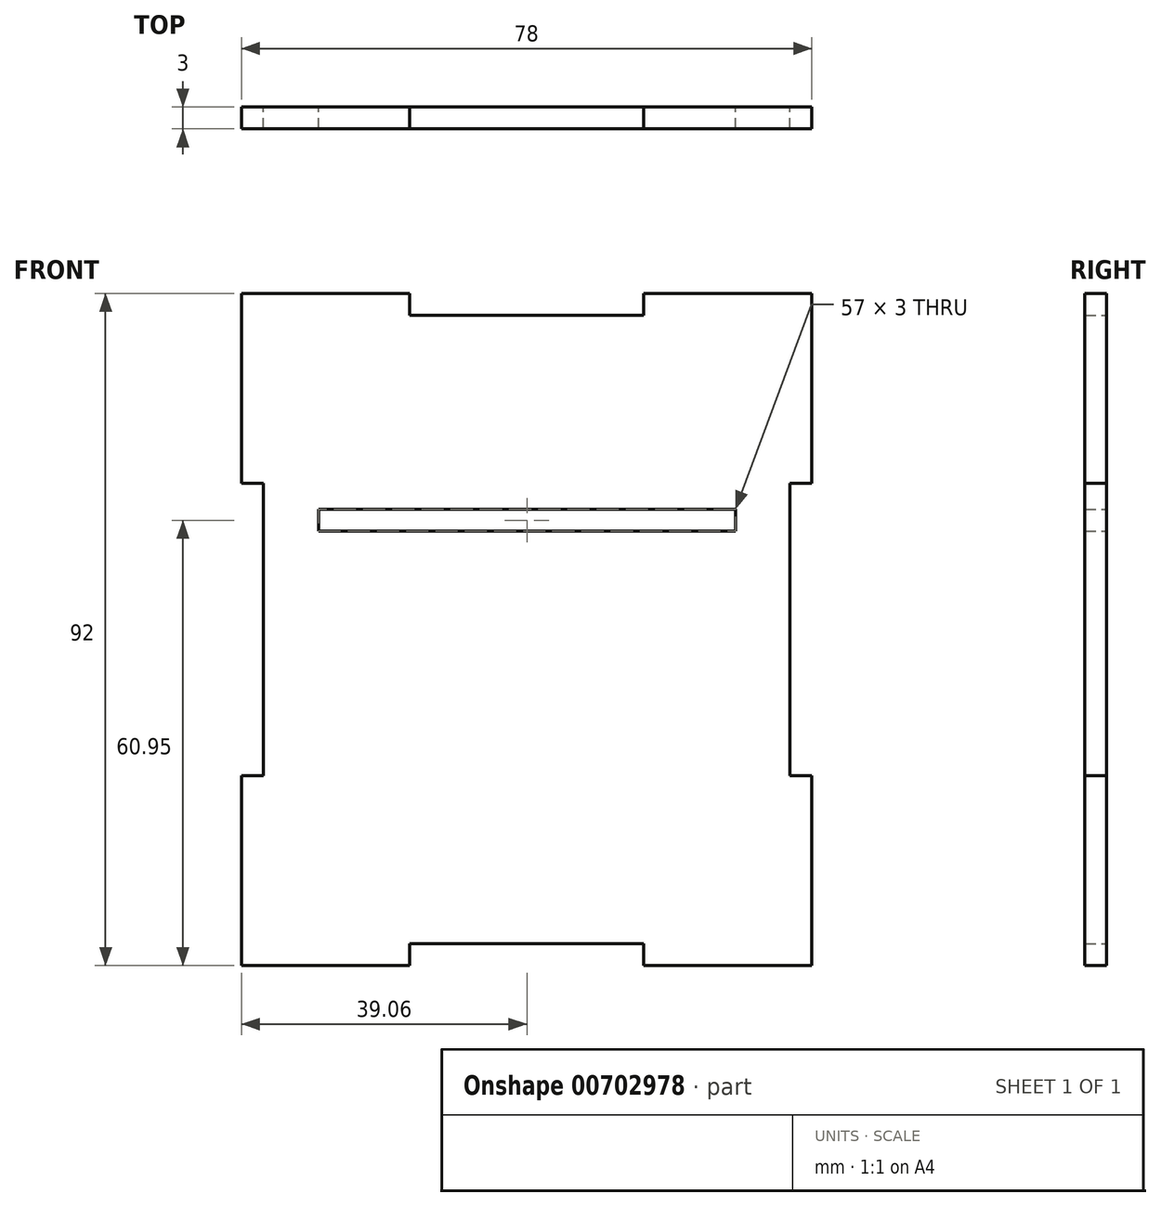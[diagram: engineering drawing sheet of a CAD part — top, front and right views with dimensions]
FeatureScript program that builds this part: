
annotation { "Feature Type Name" : "Feature", "Feature Type Description" : "" }
export const myFeature = defineFeature(function(context is Context, id is Id, definition is map)
    precondition{}
    {
        {
            var Q0;
            Q0=qCreatedBy(makeId("Front.planeOp"),FACE);
            var sketch = newSketch(context, id + "F0", { "sketchPlane" : qUnion([Q0])});
            skLineSegment(sketch, "E0.bottom", {"start": v(35.94, -39.95) * mm, "end": v(-36.06, -39.95) * mm});
            skLineSegment(sketch, "E0.top", {"start": v(35.94, 40.05) * mm, "end": v(-36.06, 40.05) * mm});
            skLineSegment(sketch, "E0.left", {"start": v(35.94, -39.95) * mm, "end": v(35.94, 40.05) * mm});
            skLineSegment(sketch, "E0.right", {"start": v(-36.06, -39.95) * mm, "end": v(-36.06, 40.05) * mm});
            skPoint(sketch, "E0.middle", {"position": v(-0.06, 0.05) * mm});
            skLineSegment(sketch, "E1.bottom", {"start": v(-36.06, 40.05) * mm, "end": v(-16.06, 40.05) * mm, "construction": true});
            skLineSegment(sketch, "E1.top", {"start": v(-36.06, 20.05) * mm, "end": v(-16.06, 20.05) * mm, "construction": true});
            skLineSegment(sketch, "E1.left", {"start": v(-36.06, 40.05) * mm, "end": v(-36.06, 20.05) * mm, "construction": true});
            skLineSegment(sketch, "E1.right", {"start": v(-16.06, 40.05) * mm, "end": v(-16.06, 20.05) * mm, "construction": true});
            skLineSegment(sketch, "E2.bottom", {"start": v(35.94, -39.95) * mm, "end": v(15.94, -39.95) * mm, "construction": true});
            skLineSegment(sketch, "E2.top", {"start": v(35.94, -19.95) * mm, "end": v(15.94, -19.95) * mm, "construction": true});
            skLineSegment(sketch, "E2.left", {"start": v(35.94, -39.95) * mm, "end": v(35.94, -19.95) * mm, "construction": true});
            skLineSegment(sketch, "E2.right", {"start": v(15.94, -39.95) * mm, "end": v(15.94, -19.95) * mm, "construction": true});
            skLineSegment(sketch, "E3.bottom", {"start": v(35.94, 40.05) * mm, "end": v(15.94, 40.05) * mm, "construction": true});
            skLineSegment(sketch, "E3.top", {"start": v(35.94, 20.05) * mm, "end": v(15.94, 20.05) * mm, "construction": true});
            skLineSegment(sketch, "E3.left", {"start": v(35.94, 40.05) * mm, "end": v(35.94, 20.05) * mm, "construction": true});
            skLineSegment(sketch, "E3.right", {"start": v(15.94, 40.05) * mm, "end": v(15.94, 20.05) * mm, "construction": true});
            skLineSegment(sketch, "E4.bottom", {"start": v(-36.06, -39.95) * mm, "end": v(-16.06, -39.95) * mm, "construction": true});
            skLineSegment(sketch, "E4.top", {"start": v(-36.06, -19.95) * mm, "end": v(-16.06, -19.95) * mm, "construction": true});
            skLineSegment(sketch, "E4.left", {"start": v(-36.06, -39.95) * mm, "end": v(-36.06, -19.95) * mm, "construction": true});
            skLineSegment(sketch, "E4.right", {"start": v(-16.06, -39.95) * mm, "end": v(-16.06, -19.95) * mm, "construction": true});
            skLineSegment(sketch, "E5.bottom", {"start": v(-16.06, 40.05) * mm, "end": v(-36.06, 40.05) * mm});
            skLineSegment(sketch, "E5.top", {"start": v(-16.06, 43.05) * mm, "end": v(-36.06, 43.05) * mm});
            skLineSegment(sketch, "E5.left", {"start": v(-16.06, 40.05) * mm, "end": v(-16.06, 43.05) * mm});
            skLineSegment(sketch, "E5.right", {"start": v(-36.06, 40.05) * mm, "end": v(-36.06, 43.05) * mm});
            skLineSegment(sketch, "E6.bottom", {"start": v(35.94, 40.05) * mm, "end": v(15.94, 40.05) * mm});
            skLineSegment(sketch, "E6.top", {"start": v(35.94, 43.05) * mm, "end": v(15.94, 43.05) * mm});
            skLineSegment(sketch, "E6.left", {"start": v(35.94, 40.05) * mm, "end": v(35.94, 43.05) * mm});
            skLineSegment(sketch, "E6.right", {"start": v(15.94, 40.05) * mm, "end": v(15.94, 43.05) * mm});
            skLineSegment(sketch, "E7.bottom", {"start": v(35.94, 40.05) * mm, "end": v(38.94, 40.05) * mm});
            skLineSegment(sketch, "E7.top", {"start": v(35.94, 20.05) * mm, "end": v(38.94, 20.05) * mm});
            skLineSegment(sketch, "E7.left", {"start": v(35.94, 40.05) * mm, "end": v(35.94, 20.05) * mm});
            skLineSegment(sketch, "E7.right", {"start": v(38.94, 40.05) * mm, "end": v(38.94, 20.05) * mm});
            skLineSegment(sketch, "E8.bottom", {"start": v(35.94, -19.95) * mm, "end": v(38.94, -19.95) * mm});
            skLineSegment(sketch, "E8.top", {"start": v(35.94, -39.95) * mm, "end": v(38.94, -39.95) * mm});
            skLineSegment(sketch, "E8.left", {"start": v(35.94, -19.95) * mm, "end": v(35.94, -39.95) * mm});
            skLineSegment(sketch, "E8.right", {"start": v(38.94, -19.95) * mm, "end": v(38.94, -39.95) * mm});
            skLineSegment(sketch, "E9.bottom", {"start": v(-36.06, 40.05) * mm, "end": v(-39.06, 40.05) * mm});
            skLineSegment(sketch, "E9.top", {"start": v(-36.06, 20.05) * mm, "end": v(-39.06, 20.05) * mm});
            skLineSegment(sketch, "E9.left", {"start": v(-36.06, 40.05) * mm, "end": v(-36.06, 20.05) * mm});
            skLineSegment(sketch, "E9.right", {"start": v(-39.06, 40.05) * mm, "end": v(-39.06, 20.05) * mm});
            skLineSegment(sketch, "E10.bottom", {"start": v(-36.06, -19.95) * mm, "end": v(-39.06, -19.95) * mm});
            skLineSegment(sketch, "E10.top", {"start": v(-36.06, -39.95) * mm, "end": v(-39.06, -39.95) * mm});
            skLineSegment(sketch, "E10.left", {"start": v(-36.06, -19.95) * mm, "end": v(-36.06, -39.95) * mm});
            skLineSegment(sketch, "E10.right", {"start": v(-39.06, -19.95) * mm, "end": v(-39.06, -39.95) * mm});
            skLineSegment(sketch, "E11.bottom", {"start": v(-36.06, -39.95) * mm, "end": v(-16.06, -39.95) * mm});
            skLineSegment(sketch, "E11.top", {"start": v(-36.06, -42.95) * mm, "end": v(-16.06, -42.95) * mm});
            skLineSegment(sketch, "E11.left", {"start": v(-36.06, -39.95) * mm, "end": v(-36.06, -42.95) * mm});
            skLineSegment(sketch, "E11.right", {"start": v(-16.06, -39.95) * mm, "end": v(-16.06, -42.95) * mm});
            skLineSegment(sketch, "E12.bottom", {"start": v(15.94, -39.95) * mm, "end": v(35.94, -39.95) * mm});
            skLineSegment(sketch, "E12.top", {"start": v(15.94, -42.95) * mm, "end": v(35.94, -42.95) * mm});
            skLineSegment(sketch, "E12.left", {"start": v(15.94, -39.95) * mm, "end": v(15.94, -42.95) * mm});
            skLineSegment(sketch, "E12.right", {"start": v(35.94, -39.95) * mm, "end": v(35.94, -42.95) * mm});
            skLineSegment(sketch, "E13.top", {"start": v(-36.06, 43.05) * mm, "end": v(-39.06, 43.05) * mm});
            skLineSegment(sketch, "E13.right", {"start": v(-39.06, 40.05) * mm, "end": v(-39.06, 43.05) * mm});
            skLineSegment(sketch, "E14.top", {"start": v(35.94, 43.05) * mm, "end": v(38.94, 43.05) * mm});
            skLineSegment(sketch, "E14.right", {"start": v(38.94, 40.05) * mm, "end": v(38.94, 43.05) * mm});
            skLineSegment(sketch, "E15.top", {"start": v(35.94, -42.95) * mm, "end": v(38.94, -42.95) * mm});
            skLineSegment(sketch, "E15.right", {"start": v(38.94, -39.95) * mm, "end": v(38.94, -42.95) * mm});
            skLineSegment(sketch, "E16.top", {"start": v(-36.06, -42.95) * mm, "end": v(-39.06, -42.95) * mm});
            skLineSegment(sketch, "E16.right", {"start": v(-39.06, -39.95) * mm, "end": v(-39.06, -42.95) * mm});
            skLineSegment(sketch, "E17", {"start": v(35.94, 43.05) * mm, "end": v(35.94, 46.05) * mm});
            skLineSegment(sketch, "E18", {"start": v(35.94, 46.05) * mm, "end": v(15.94, 46.05) * mm});
            skLineSegment(sketch, "E19", {"start": v(15.94, 46.05) * mm, "end": v(15.94, 43.05) * mm});
            skLineSegment(sketch, "E20", {"start": v(-39.06, 43.05) * mm, "end": v(-39.06, 46.05) * mm});
            skLineSegment(sketch, "E21", {"start": v(-39.06, 46.05) * mm, "end": v(-16.06, 46.05) * mm});
            skLineSegment(sketch, "E22", {"start": v(-16.06, 46.05) * mm, "end": v(-16.06, 43.05) * mm});
            skLineSegment(sketch, "E23", {"start": v(-16.06, 43.05) * mm, "end": v(15.94, 43.05) * mm});
            skLineSegment(sketch, "E24", {"start": v(38.94, -42.95) * mm, "end": v(38.94, -45.95) * mm});
            skLineSegment(sketch, "E25", {"start": v(38.94, -45.95) * mm, "end": v(15.94, -45.95) * mm});
            skLineSegment(sketch, "E26", {"start": v(-39.06, -42.95) * mm, "end": v(-39.06, -45.95) * mm});
            skLineSegment(sketch, "E27", {"start": v(-39.06, -45.95) * mm, "end": v(-16.06, -45.95) * mm});
            skLineSegment(sketch, "E28", {"start": v(-16.06, -45.95) * mm, "end": v(-16.06, -42.95) * mm});
            skLineSegment(sketch, "E29", {"start": v(-16.06, -42.95) * mm, "end": v(15.94, -42.95) * mm});
            skLineSegment(sketch, "E30", {"start": v(35.94, 46.05) * mm, "end": v(38.94, 46.05) * mm});
            skLineSegment(sketch, "E31", {"start": v(38.94, 46.05) * mm, "end": v(38.94, 43.05) * mm});
            skLineSegment(sketch, "E32", {"start": v(0, 0) * mm, "end": v(0, 15) * mm, "construction": true});
            skLineSegment(sketch, "E33.bottom", {"start": v(28.5, 13.5) * mm, "end": v(-28.5, 13.5) * mm});
            skLineSegment(sketch, "E33.top", {"start": v(28.5, 16.5) * mm, "end": v(-28.5, 16.5) * mm});
            skLineSegment(sketch, "E33.left", {"start": v(28.5, 13.5) * mm, "end": v(28.5, 16.5) * mm});
            skLineSegment(sketch, "E33.right", {"start": v(-28.5, 13.5) * mm, "end": v(-28.5, 16.5) * mm});
            skPoint(sketch, "E33.middle", {"position": v(0, 15) * mm});
            skLineSegment(sketch, "E34", {"start": v(15.94, -42.95) * mm, "end": v(15.94, -45.95) * mm});
            skSolve(sketch);
        }
        {
            var Q0;
            Q0 = qSketchRegion(id + "F0", true);
            extrude(context, id + "F1", {"entities" : qUnion([Q0]), "depth" : 3 * mm, "offsetDistance" : 25 * mm});
        }
    });
